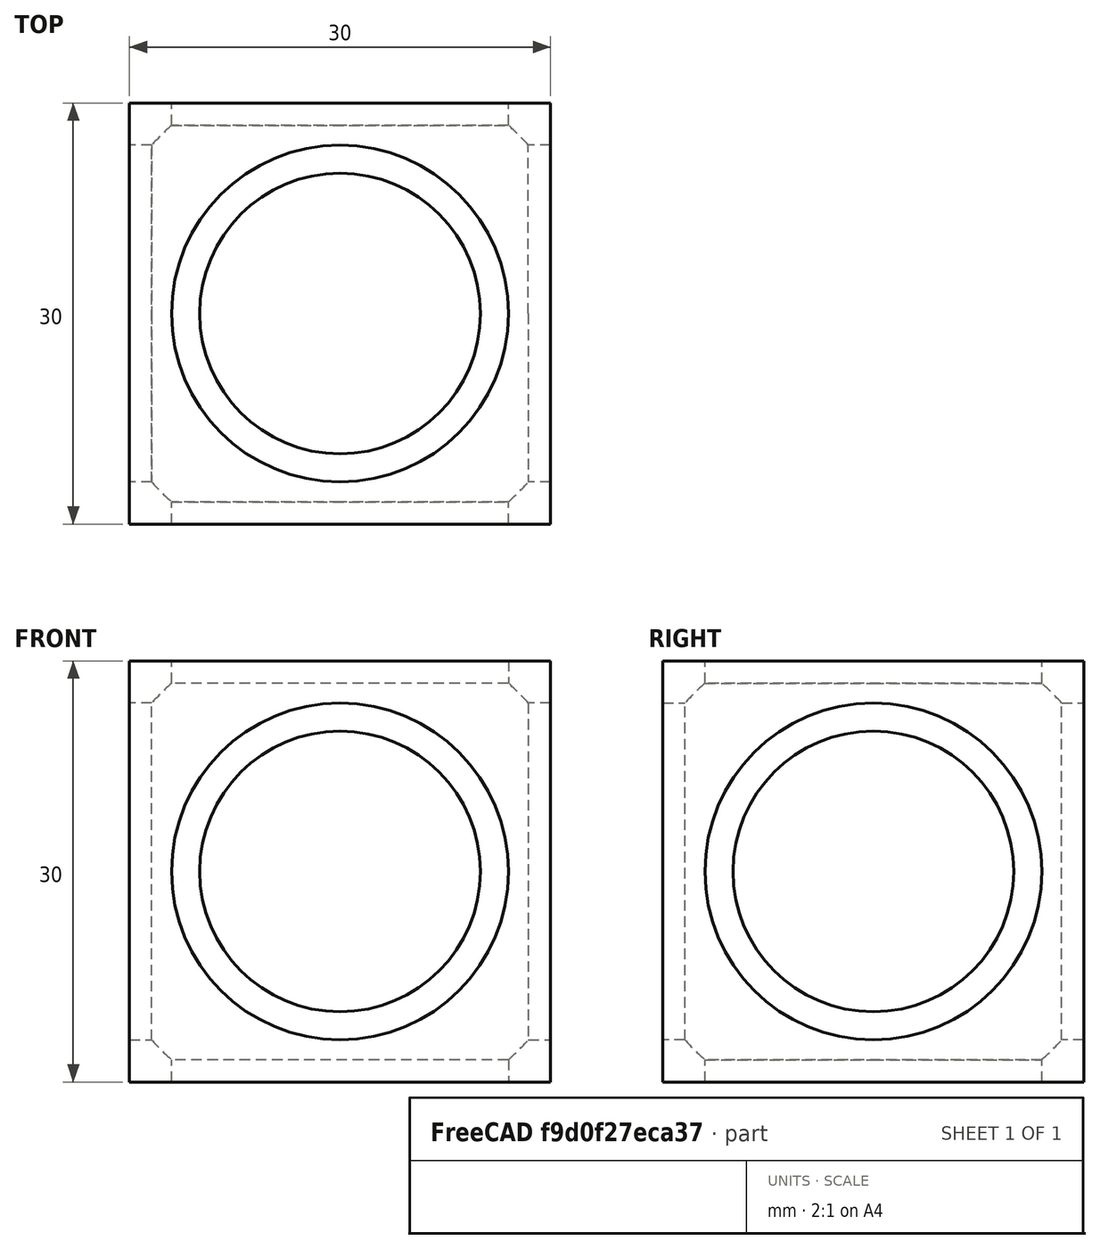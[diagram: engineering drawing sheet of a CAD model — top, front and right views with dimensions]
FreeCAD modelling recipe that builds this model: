
FCSTD DOCUMENT  (FreeCAD 0.21R33694 (Git))
Label: npatris_repte3
License: All rights reserved
LicenseURL: https://en.wikipedia.org/wiki/All_rights_reserved
objects: Part::Cylinder×3, Part::Cut×2, Part::Sphere×2, Part::Box×1, Part::MultiFuse×1
note: 9 computed .brp shape members not serialized (recipe doc carries the construction recipe); baked Part::Feature solids carry a one-line shape summary decoded from their .brp

FEATURE [Part::Box] Box  label="Cub_base"
  AttacherType = Attacher::AttachEngine3D
  Height = 30
  Length = 30
  Width = 30
FEATURE [Part::Cylinder] Cylinder  label="Cilindre_1"
  Angle = 360
  AttacherType = Attacher::AttachEngine3D
  FirstAngle = 0
  Height = 36
  Placement = pos=(-3,15,15) rot=(0,1,0;1.5708rad)
  Radius = 12
  SecondAngle = 0
FEATURE [Part::Cylinder] Cylinder001  label="Cilindre_2"
  Angle = 360
  AttacherType = Attacher::AttachEngine3D
  FirstAngle = 0
  Height = 36
  Placement = pos=(15,33,15) rot=(0.57735,0.57735,-0.57735;2.0944rad)
  Radius = 12
  SecondAngle = 0
FEATURE [Part::Cylinder] Cylinder002  label="Cilindre_3"
  Angle = 360
  AttacherType = Attacher::AttachEngine3D
  FirstAngle = 0
  Height = 36
  Placement = pos=(15,15,33) rot=(1,0,0;3.14159rad)
  Radius = 12
  SecondAngle = 0
FEATURE [Part::MultiFuse] Fusion  label="Unió_dels_tres_cilindres"
  Shapes = -> [Cylinder,Cylinder001,Cylinder002]
FEATURE [Part::Cut] Cut  label="Cub_amb_cilindres_restats"
  Base = -> Box
  Tool = -> Fusion
FEATURE [Part::Sphere] Sphere  label="Esfera_per_restar"
  Angle1 = -90
  Angle2 = 90
  Angle3 = 360
  AttacherType = Attacher::AttachEngine3D
  Placement = pos=(15,15,15) rot=(0,0,1;0rad)
  Radius = 18
FEATURE [Part::Cut] Cut001  label="Cub_amb_esfera_ja_restada"
  Base = -> Cut
  Tool = -> Sphere
FEATURE [Part::Sphere] Sphere001  label="Esfera_interior"
  Angle1 = -90
  Angle2 = 90
  Angle3 = 360
  AttacherType = Attacher::AttachEngine3D
  Placement = pos=(15,15,15) rot=(0,0,1;0rad)
  Radius = 10
